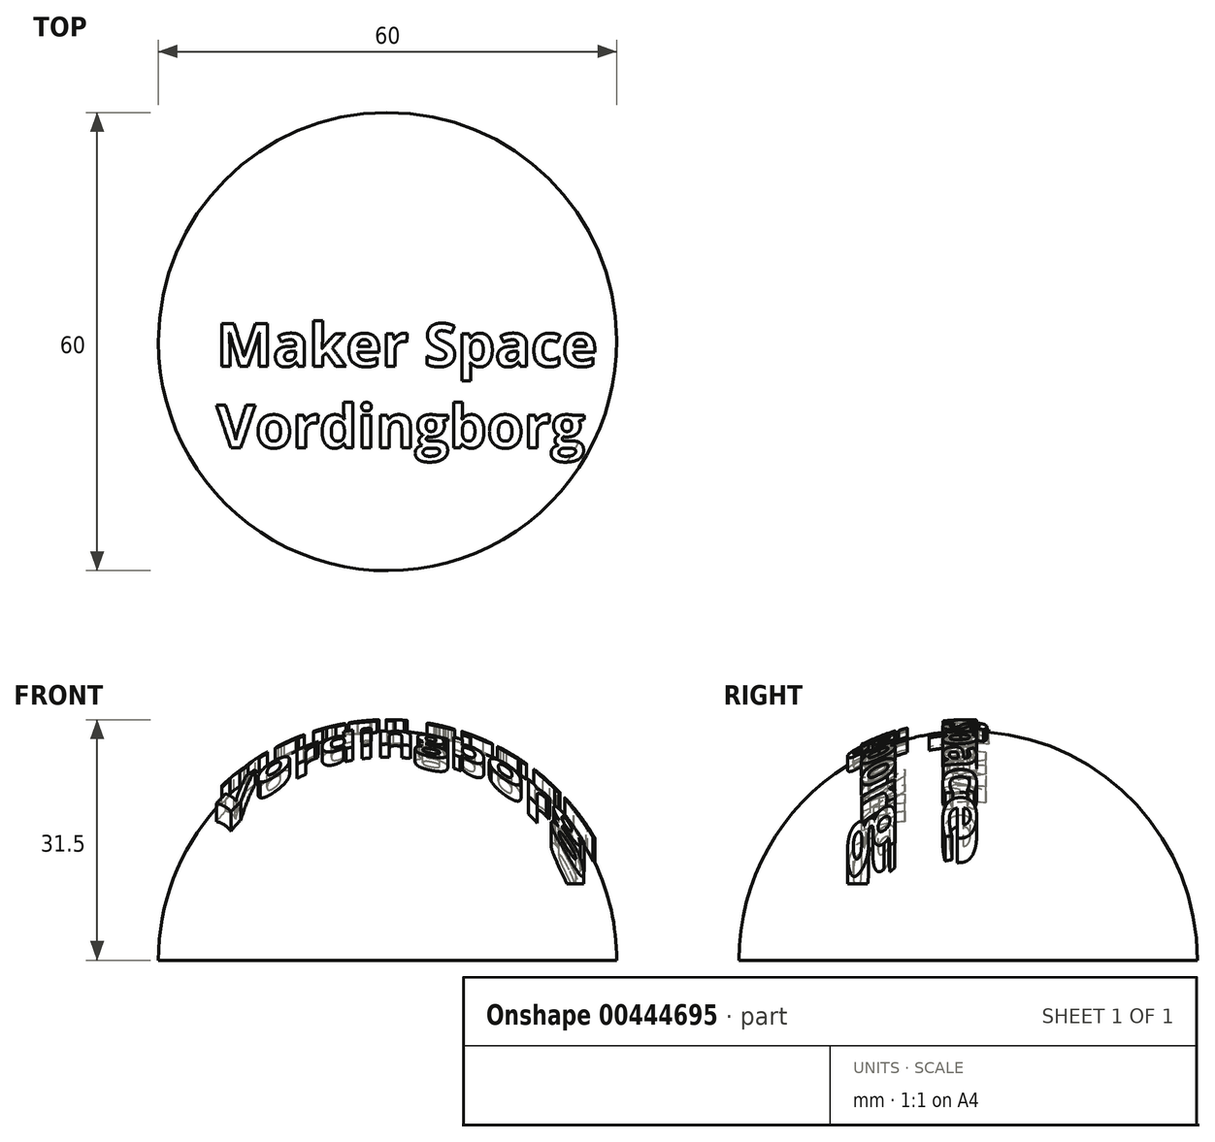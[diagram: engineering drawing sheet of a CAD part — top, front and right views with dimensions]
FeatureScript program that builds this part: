
annotation { "Feature Type Name" : "Feature", "Feature Type Description" : "" }
export const myFeature = defineFeature(function(context is Context, id is Id, definition is map)
    precondition{}
    {
        {
            var Q0;
            Q0=qCreatedBy(makeId("Front.planeOp"),FACE);
            var sketch = newSketch(context, id + "F0", { "sketchPlane" : qUnion([Q0])});
            skArc(sketch, "E0", {"start": v(30, 0) * mm, "mid": v(21.21, 21.21) * mm, "end": v(0, 30) * mm});
            skLineSegment(sketch, "E1", {"start": v(0, 0) * mm, "end": v(30, 0) * mm});
            skLineSegment(sketch, "E2", {"start": v(0, 0) * mm, "end": v(0, 30) * mm});
            skSolve(sketch);
        }
        {
            var Q0;
            Q0=qCreatedBy(makeId("Top.planeOp"),FACE);
            cPlane(context, id + "F1", {"entities" : qUnion([Q0]), "cplaneType" : CPlaneType.OFFSET, "offset" : 35 * mm, "width" : 150 * mm, "height" : 150 * mm});
        }
        {
            var Q0;
            Q0=qCreatedBy(id+"F1.planeOp",FACE);
            var sketch = newSketch(context, id + "F2", { "sketchPlane" : qUnion([Q0])});
            skText(sketch, "E3", { "text": "Maker Space\nVordingborg", "fontName": "OpenSans-Bold.ttf"});
            const initialGuessF2  = {"E3": [-0.0224, -0.00325, 1, 0, 0.00564]};
            skSetInitialGuess(sketch, initialGuessF2);
            skSolve(sketch);
        }
        {
            var Q0;
            Q0=makeQuery(id+"F0.imprint","IMPRINT",FACE,{"disambiguationData":[TD([[makeQuery(id+"F0.imprint","IMPRINT",EDGE,{"derivedFrom":sQuery(id+"F0.wireOp",EDGE,"E0")}),1.0]])]});
            var Q1;
            Q1=sQuery(id+"F0.wireOp",EDGE,"E2");
            revolve(context, id + "F3", {"entities" : qUnion([Q0]), "axis" : qUnion([Q1]), "revolveType" : RevolveType.FULL});
        }
        {
            var Q0;
            Q0 = qSketchRegion(id + "F2", true);
            extrude(context, id + "F4", {"entities" : qUnion([Q0]), "operationType" : NewBodyOperationType.ADD, "oppositeDirection" : true, "depth" : 25 * mm});
        }
        {
            var Q0;
            Q0=qCreatedBy(makeId("Front.planeOp"),FACE);
            var sketch = newSketch(context, id + "F5", { "sketchPlane" : qUnion([Q0])});
            skArc(sketch, "E4", {"start": v(31.5, 0) * mm, "mid": v(22.27, 22.27) * mm, "end": v(0, 31.5) * mm});
            skArc(sketch, "E5", {"start": v(47.94, 0) * mm, "mid": v(33.9, 33.9) * mm, "end": v(0, 47.94) * mm});
            skLineSegment(sketch, "E6", {"start": v(31.5, 0) * mm, "end": v(47.94, 0) * mm});
            skLineSegment(sketch, "E7", {"start": v(0, 31.5) * mm, "end": v(0, 47.94) * mm});
            skSolve(sketch);
        }
        {
            var Q0;
            Q0=makeQuery(id+"F5.imprint","IMPRINT",FACE,{"disambiguationData":[TD([[makeQuery(id+"F5.imprint","IMPRINT",EDGE,{"derivedFrom":sQuery(id+"F5.wireOp",EDGE,"E4")}),-1.0]])]});
            var Q1;
            Q1=sQuery(id+"F5.wireOp",EDGE,"E7");
            revolve(context, id + "F6", {"operationType" : NewBodyOperationType.REMOVE, "entities" : qUnion([Q0]), "axis" : qUnion([Q1]), "revolveType" : RevolveType.FULL, "oppositeDirection" : true});
        }
    });
